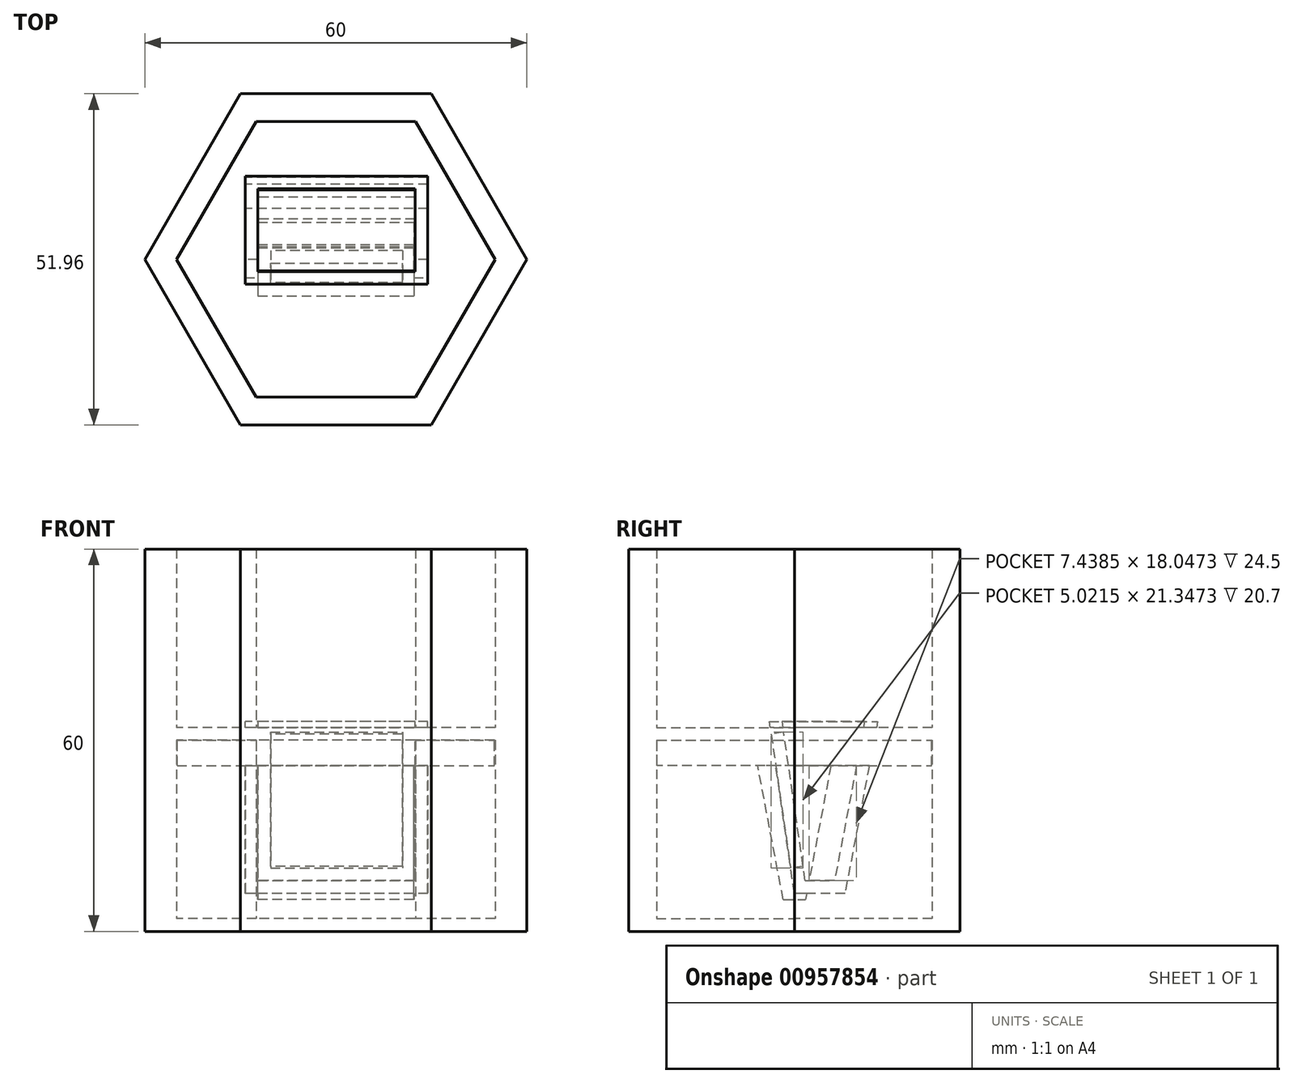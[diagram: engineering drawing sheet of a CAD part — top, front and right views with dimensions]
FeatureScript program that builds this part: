
annotation { "Feature Type Name" : "Feature", "Feature Type Description" : "" }
export const myFeature = defineFeature(function(context is Context, id is Id, definition is map)
    precondition{}
    {
        {
            var Q0;
            Q0=qCreatedBy(makeId("Top.planeOp"),FACE);
            var sketch = newSketch(context, id + "F0", { "sketchPlane" : qUnion([Q0])});
            skCircle(sketch, "E0.cCircle", {"center": v(0, 0) * mm, "radius": 30 * mm, "construction": true});
            skLineSegment(sketch, "E0.0", {"start": v(30, 0) * mm, "end": v(15, -25.98) * mm});
            skLineSegment(sketch, "E0.1", {"start": v(15, -25.98) * mm, "end": v(-15, -25.98) * mm});
            skLineSegment(sketch, "E0.2", {"start": v(-15, -25.98) * mm, "end": v(-30, 0) * mm});
            skLineSegment(sketch, "E0.3", {"start": v(-30, 0) * mm, "end": v(-15, 25.98) * mm});
            skLineSegment(sketch, "E0.4", {"start": v(-15, 25.98) * mm, "end": v(15, 25.98) * mm});
            skLineSegment(sketch, "E0.5", {"start": v(15, 25.98) * mm, "end": v(30, 0) * mm});
            skCircle(sketch, "E1.cCircle", {"center": v(0, 0) * mm, "radius": 25 * mm, "construction": true});
            skLineSegment(sketch, "E1.0", {"start": v(-25, 0) * mm, "end": v(-12.5, 21.65) * mm});
            skLineSegment(sketch, "E1.1", {"start": v(-12.5, 21.65) * mm, "end": v(12.5, 21.65) * mm});
            skLineSegment(sketch, "E1.2", {"start": v(12.5, 21.65) * mm, "end": v(25, 0) * mm});
            skLineSegment(sketch, "E1.3", {"start": v(25, 0) * mm, "end": v(12.5, -21.65) * mm});
            skLineSegment(sketch, "E1.4", {"start": v(12.5, -21.65) * mm, "end": v(-12.5, -21.65) * mm});
            skLineSegment(sketch, "E1.5", {"start": v(-12.5, -21.65) * mm, "end": v(-25, 0) * mm});
            skSolve(sketch);
        }
        {
            var Q0;
            Q0=makeQuery(id+"F0.imprint","IMPRINT",FACE,{"disambiguationData":[TD([[makeQuery(id+"F0.imprint","IMPRINT",EDGE,{"derivedFrom":sQuery(id+"F0.wireOp",EDGE,"E0.0")}),-1.0]])]});
            extrude(context, id + "F1", {"entities" : qUnion([Q0]), "endBound" : BoundingType.SYMMETRIC, "depth" : 60 * mm, "offsetDistance" : 25 * mm});
        }
        {
            var Q0;
            Q0=makeQuery(id+"F1.opExtrude","CAP_VERTEX",VERTEX,{"disambiguationData":[OSD([sQuery(id+"F0.wireOp",EDGE,"E0.4"),sQuery(id+"F0.wireOp",EDGE,"E0.5")])],"isStart":true});
            var Q1;
            Q1=makeQuery(id+"F1.opExtrude","CAP_VERTEX",VERTEX,{"disambiguationData":[OSD([sQuery(id+"F0.wireOp",EDGE,"E0.2"),sQuery(id+"F0.wireOp",EDGE,"E0.3")])],"isStart":true});
            var Q2;
            Q2=makeQuery(id+"F1.opExtrude","CAP_VERTEX",VERTEX,{"disambiguationData":[OSD([sQuery(id+"F0.wireOp",EDGE,"E0.0"),sQuery(id+"F0.wireOp",EDGE,"E0.1")])],"isStart":true});
            cPlane(context, id + "F2", {"entities" : qUnion([Q0, Q1, Q2]), "cplaneType" : CPlaneType.THREE_POINT, "offset" : 25 * mm, "width" : 150 * mm, "height" : 150 * mm});
        }
        {
            var Q0;
            Q0=qCreatedBy(id+"F2.planeOp",FACE);
            var sketch = newSketch(context, id + "F3", { "sketchPlane" : qUnion([Q0])});
            skLineSegment(sketch, "E2.0", {"start": v(-12.5, -21.65) * mm, "end": v(12.5, -21.65) * mm});
            skLineSegment(sketch, "E3.0", {"start": v(12.5, -21.65) * mm, "end": v(25, 0) * mm});
            skLineSegment(sketch, "E4.0", {"start": v(25, 0) * mm, "end": v(12.5, 21.65) * mm});
            skPoint(sketch, "E5.0", {"position": v(0, 21.65) * mm});
            skLineSegment(sketch, "E6.0", {"start": v(-12.5, 21.65) * mm, "end": v(-25, 0) * mm});
            skLineSegment(sketch, "E7.0", {"start": v(-25, 0) * mm, "end": v(-12.5, -21.65) * mm});
            skLineSegment(sketch, "E8.0", {"start": v(12.5, 21.65) * mm, "end": v(-12.5, 21.65) * mm});
            skSolve(sketch);
        }
        {
            var Q0;
            Q0=makeQuery(id+"F3.imprint","IMPRINT",FACE,{"disambiguationData":[TD([[makeQuery(id+"F3.imprint","IMPRINT",EDGE,{"derivedFrom":sQuery(id+"F3.wireOp",EDGE,"E2.0")}),1.0]])]});
            extrude(context, id + "F4", {"entities" : qUnion([Q0]), "operationType" : NewBodyOperationType.ADD, "oppositeDirection" : true, "depth" : 2 * mm, "offsetDistance" : 25 * mm});
        }
        {
            var Q0;
            Q0=qCreatedBy(makeId("Top.planeOp"),FACE);
            var sketch = newSketch(context, id + "F5", { "sketchPlane" : qUnion([Q0])});
            skLineSegment(sketch, "E9.0.0", {"start": v(30, 0) * mm, "end": v(15, 25.98) * mm});
            skLineSegment(sketch, "E9.0.1", {"start": v(15, 25.98) * mm, "end": v(-15, 25.98) * mm});
            skLineSegment(sketch, "E9.0.2", {"start": v(-15, 25.98) * mm, "end": v(-30, 0) * mm});
            skLineSegment(sketch, "E9.0.3", {"start": v(-30, 0) * mm, "end": v(-15, -25.98) * mm});
            skLineSegment(sketch, "E9.0.4", {"start": v(-15, -25.98) * mm, "end": v(15, -25.98) * mm});
            skLineSegment(sketch, "E9.0.5", {"start": v(15, -25.98) * mm, "end": v(30, 0) * mm});
            skCircle(sketch, "E10.cCircle", {"center": v(0, 0) * mm, "radius": 24.9 * mm, "construction": true});
            skLineSegment(sketch, "E10.0", {"start": v(-24.9, 0) * mm, "end": v(-12.45, 21.56) * mm});
            skLineSegment(sketch, "E10.1", {"start": v(-12.45, 21.56) * mm, "end": v(12.45, 21.56) * mm});
            skLineSegment(sketch, "E10.2", {"start": v(12.45, 21.56) * mm, "end": v(24.9, 0) * mm});
            skLineSegment(sketch, "E10.3", {"start": v(24.9, 0) * mm, "end": v(12.45, -21.56) * mm});
            skLineSegment(sketch, "E10.4", {"start": v(12.45, -21.56) * mm, "end": v(-12.45, -21.56) * mm});
            skLineSegment(sketch, "E10.5", {"start": v(-12.45, -21.56) * mm, "end": v(-24.9, 0) * mm});
            skSolve(sketch);
        }
        {
            var Q0;
            Q0=makeQuery(id+"F5.imprint","IMPRINT",FACE,{"disambiguationData":[TD([[makeQuery(id+"F5.imprint","IMPRINT",EDGE,{"derivedFrom":sQuery(id+"F5.wireOp",EDGE,"E10.0")}),-1.0]])]});
            extrude(context, id + "F6", {"entities" : qUnion([Q0]), "oppositeDirection" : true, "depth" : 4 * mm, "offsetDistance" : 25 * mm});
        }
        {
            var Q0;
            Q0=makeQuery(id+"F5.imprint","IMPRINT",FACE,{"disambiguationData":[TD([[makeQuery(id+"F5.imprint","IMPRINT",EDGE,{"derivedFrom":sQuery(id+"F5.wireOp",EDGE,"E9.0.0")}),1.0]])]});
            var Q1;
            Q1=makeQuery(id+"F5.imprint","IMPRINT",FACE,{"disambiguationData":[TD([[makeQuery(id+"F5.imprint","IMPRINT",EDGE,{"derivedFrom":sQuery(id+"F5.wireOp",EDGE,"E10.0")}),-1.0]])]});
            extrude(context, id + "F7", {"entities" : qUnion([Q0, Q1]), "operationType" : NewBodyOperationType.ADD, "depth" : 2 * mm, "offsetDistance" : 25 * mm});
        }
        {
            var Q0;
            Q0=qCreatedBy(makeId("Top.planeOp"),FACE);
            var sketch = newSketch(context, id + "F8", { "sketchPlane" : qUnion([Q0])});
            skLineSegment(sketch, "E11.bottom", {"start": v(12.25, 6.5) * mm, "end": v(-12.25, 6.5) * mm});
            skLineSegment(sketch, "E11.top", {"start": v(12.25, -6.5) * mm, "end": v(-12.25, -6.5) * mm});
            skLineSegment(sketch, "E11.left", {"start": v(12.25, 6.5) * mm, "end": v(12.25, -6.5) * mm});
            skLineSegment(sketch, "E11.right", {"start": v(-12.25, 6.5) * mm, "end": v(-12.25, -6.5) * mm});
            skPoint(sketch, "E11.middle", {"position": v(0, 0) * mm});
            skSolve(sketch);
        }
        {
            var Q0;
            Q0=qCreatedBy(makeId("Top.planeOp"),FACE);
            cPlane(context, id + "F9", {"entities" : qUnion([Q0]), "cplaneType" : CPlaneType.OFFSET, "offset" : 25 * mm, "oppositeDirection" : true, "width" : 150 * mm, "height" : 150 * mm});
        }
        {
            var Q0;
            Q0=qCreatedBy(id+"F9.planeOp",FACE);
            var sketch = newSketch(context, id + "F10", { "sketchPlane" : qUnion([Q0])});
            skLineSegment(sketch, "E12.bottom", {"start": v(12.25, -1.75) * mm, "end": v(-12.25, -1.75) * mm});
            skLineSegment(sketch, "E12.top", {"start": v(12.25, 1.75) * mm, "end": v(-12.25, 1.75) * mm});
            skLineSegment(sketch, "E12.left", {"start": v(12.25, -1.75) * mm, "end": v(12.25, 1.75) * mm});
            skLineSegment(sketch, "E12.right", {"start": v(-12.25, -1.75) * mm, "end": v(-12.25, 1.75) * mm});
            skPoint(sketch, "E12.middle", {"position": v(0, 0) * mm});
            skSolve(sketch);
        }
        {
            var Q0;
            Q0=sQuery(id+"F8.wireOp",VERTEX,"E11.bottom.end");
            var Q1;
            Q1=sQuery(id+"F8.wireOp",VERTEX,"E11.top.end");
            var Q2;
            Q2=sQuery(id+"F10.wireOp",VERTEX,"E12.bottom.end");
            cPlane(context, id + "F11", {"entities" : qUnion([Q0, Q1, Q2]), "cplaneType" : CPlaneType.THREE_POINT, "offset" : 25 * mm, "width" : 150 * mm, "height" : 150 * mm});
        }
        {
            var Q0;
            Q0=qCreatedBy(id+"F11.planeOp",FACE);
            var sketch = newSketch(context, id + "F12", { "sketchPlane" : qUnion([Q0])});
            skLineSegment(sketch, "E13.0", {"start": v(-6.5, 0) * mm, "end": v(6.5, 0) * mm});
            skLineSegment(sketch, "E14.0", {"start": v(1.75, -25) * mm, "end": v(-1.75, -25) * mm});
            skLineSegment(sketch, "E15", {"start": v(-6.5, 0) * mm, "end": v(-1.75, -25) * mm});
            skLineSegment(sketch, "E16", {"start": v(1.75, -25) * mm, "end": v(6.5, 0) * mm});
            skSolve(sketch);
        }
        {
            var Q0;
            Q0=makeQuery(id+"F12.imprint","IMPRINT",FACE,{"disambiguationData":[TD([[makeQuery(id+"F12.imprint","IMPRINT",EDGE,{"derivedFrom":sQuery(id+"F12.wireOp",EDGE,"E13.0")}),-1.0]])]});
            extrude(context, id + "F13", {"entities" : qUnion([Q0]), "oppositeDirection" : true, "depth" : 24.5 * mm, "offsetDistance" : 25 * mm});
        }
        {
            var Q0;
            Q0=qCreatedBy(id+"F11.planeOp",FACE);
            var sketch = newSketch(context, id + "F14", { "sketchPlane" : qUnion([Q0])});
            skLineSegment(sketch, "E17.0", {"start": v(-11.07, 2.96) * mm, "end": v(1.93, 2.96) * mm});
            skLineSegment(sketch, "E18.0", {"start": v(-1.7, -22.04) * mm, "end": v(-6.32, -22.05) * mm});
            skLineSegment(sketch, "E19", {"start": v(-11.07, 2.96) * mm, "end": v(-6.32, -22.05) * mm});
            skLineSegment(sketch, "E20", {"start": v(-1.7, -22.04) * mm, "end": v(1.93, 2.96) * mm});
            skLineSegment(sketch, "E21", {"start": v(-11.07, 2.96) * mm, "end": v(-13.07, 2.96) * mm});
            skLineSegment(sketch, "E22", {"start": v(-13.07, 2.96) * mm, "end": v(-7.94, -24.05) * mm});
            skLineSegment(sketch, "E23", {"start": v(-7.94, -24.05) * mm, "end": v(0, -24.04) * mm});
            skLineSegment(sketch, "E24", {"start": v(0, -24.04) * mm, "end": v(3.93, 2.96) * mm});
            skLineSegment(sketch, "E25", {"start": v(3.93, 2.96) * mm, "end": v(1.93, 2.96) * mm});
            skSolve(sketch);
        }
        {
            var Q0;
            Q0=makeQuery(id+"F14.imprint","IMPRINT",FACE,{"disambiguationData":[TD([[makeQuery(id+"F14.imprint","IMPRINT",EDGE,{"derivedFrom":sQuery(id+"F14.wireOp",EDGE,"E18.0")}),1.0]])]});
            extrude(context, id + "F15", {"entities" : qUnion([Q0]), "oppositeDirection" : true, "depth" : 24.7 * mm, "offsetDistance" : 25 * mm});
        }
        {
            var Q0;
            Q0=makeQuery(id+"F15.opExtrude","CAP_FACE",FACE,{"disambiguationData":[OSD([sQuery(id+"F14.wireOp",EDGE,"E18.0"),sQuery(id+"F14.wireOp",EDGE,"E19"),sQuery(id+"F14.wireOp",EDGE,"E20"),sQuery(id+"F14.wireOp",EDGE,"E21"),sQuery(id+"F14.wireOp",EDGE,"E22"),sQuery(id+"F14.wireOp",EDGE,"E23"),sQuery(id+"F14.wireOp",EDGE,"E24"),sQuery(id+"F14.wireOp",EDGE,"E25")])],"isStart":true});
            extrude(context, id + "F16", {"entities" : qUnion([Q0]), "operationType" : NewBodyOperationType.ADD, "depth" : 2 * mm, "offsetDistance" : 25 * mm});
        }
        {
            var Q0;
            Q0 = qSketchRegion(id + "F14", true);
            extrude(context, id + "F17", {"entities" : qUnion([Q0]), "operationType" : NewBodyOperationType.ADD, "depth" : 2 * mm, "offsetDistance" : 25 * mm});
        }
        {
            var Q0;
            Q0=makeQuery(id+"F15.opExtrude","CAP_VERTEX",VERTEX,{"disambiguationData":[OSD([sQuery(id+"F14.wireOp",EDGE,"E22"),sQuery(id+"F14.wireOp",EDGE,"E23")])],"isStart":false});
            var Q1;
            Q1=makeQuery(id+"F15.opExtrude","CAP_VERTEX",VERTEX,{"disambiguationData":[OSD([sQuery(id+"F14.wireOp",EDGE,"E21"),sQuery(id+"F14.wireOp",EDGE,"E22")])],"isStart":false});
            var Q2;
            Q2=makeQuery(id+"F15.opExtrude","CAP_VERTEX",VERTEX,{"disambiguationData":[OSD([sQuery(id+"F14.wireOp",EDGE,"E24"),sQuery(id+"F14.wireOp",EDGE,"E25")])],"isStart":false});
            cPlane(context, id + "F18", {"entities" : qUnion([Q0, Q1, Q2]), "cplaneType" : CPlaneType.THREE_POINT, "offset" : 25 * mm, "width" : 150 * mm, "height" : 150 * mm});
        }
        {
            var Q0;
            Q0=qCreatedBy(id+"F18.planeOp",FACE);
            var sketch = newSketch(context, id + "F19", { "sketchPlane" : qUnion([Q0])});
            skLineSegment(sketch, "E26.0", {"start": v(-13.07, 2.96) * mm, "end": v(-7.94, -24.05) * mm});
            skLineSegment(sketch, "E27.0", {"start": v(0, -24.04) * mm, "end": v(3.93, 2.96) * mm});
            skLineSegment(sketch, "E28.0", {"start": v(-7.94, -24.05) * mm, "end": v(0, -24.04) * mm});
            skLineSegment(sketch, "E29", {"start": v(-13.07, 2.96) * mm, "end": v(3.93, 2.96) * mm});
            skSolve(sketch);
        }
        {
            var Q0;
            Q0=makeQuery(id+"F19.imprint","IMPRINT",FACE,{"disambiguationData":[TD([[makeQuery(id+"F19.imprint","IMPRINT",EDGE,{"derivedFrom":sQuery(id+"F19.wireOp",EDGE,"E26.0")}),1.0]])]});
            extrude(context, id + "F20", {"entities" : qUnion([Q0]), "operationType" : NewBodyOperationType.ADD, "oppositeDirection" : true, "depth" : 2 * mm, "offsetDistance" : 25 * mm});
        }
        {
            var Q0;
            Q0=makeQuery(id+"F16.opExtrude","CAP_VERTEX",VERTEX,{"disambiguationData":[OSD([sQuery(id+"F14.wireOp",EDGE,"E24"),sQuery(id+"F14.wireOp",EDGE,"E25")])],"isStart":false});
            var Q1;
            Q1=makeQuery(id+"F20.opExtrude","CAP_VERTEX",VERTEX,{"disambiguationData":[OSD([sQuery(id+"F19.wireOp",EDGE,"E27.0"),sQuery(id+"F19.wireOp",EDGE,"E29")])],"isStart":false});
            var Q2;
            Q2=makeQuery(id+"F20.opExtrude","CAP_VERTEX",VERTEX,{"disambiguationData":[OSD([sQuery(id+"F19.wireOp",EDGE,"E27.0"),sQuery(id+"F19.wireOp",EDGE,"E28.0")])],"isStart":false});
            cPlane(context, id + "F21", {"entities" : qUnion([Q0, Q1, Q2]), "cplaneType" : CPlaneType.THREE_POINT, "offset" : 25 * mm, "width" : 150 * mm, "height" : 150 * mm});
        }
        {
            var Q0;
            Q0=qCreatedBy(id+"F21.planeOp",FACE);
            var sketch = newSketch(context, id + "F22", { "sketchPlane" : qUnion([Q0])});
            skLineSegment(sketch, "E30.0", {"start": v(-14.25, -23.79) * mm, "end": v(-14.25, 3.5) * mm});
            skLineSegment(sketch, "E31.0", {"start": v(14.45, -23.79) * mm, "end": v(14.45, 3.5) * mm});
            skLineSegment(sketch, "E32", {"start": v(-14.25, -23.79) * mm, "end": v(14.45, -23.79) * mm});
            skLineSegment(sketch, "E33", {"start": v(-14.25, 3.5) * mm, "end": v(-10.25, 3.5) * mm});
            skLineSegment(sketch, "E34", {"start": v(-10.25, -19.79) * mm, "end": v(10.45, -19.79) * mm});
            skLineSegment(sketch, "E35", {"start": v(10.45, 3.5) * mm, "end": v(14.45, 3.5) * mm});
            skLineSegment(sketch, "E36", {"start": v(-10.25, 3.5) * mm, "end": v(10.45, 3.5) * mm});
            skLineSegment(sketch, "E37", {"start": v(10.45, 1.5) * mm, "end": v(-10.25, 1.5) * mm});
            skLineSegment(sketch, "E38", {"start": v(-10.25, 1.5) * mm, "end": v(-10.25, -19.79) * mm});
            skLineSegment(sketch, "E39", {"start": v(10.45, 1.5) * mm, "end": v(10.45, -19.79) * mm});
            skSolve(sketch);
        }
        {
            var Q0;
            Q0=makeQuery(id+"F22.imprint","IMPRINT",FACE,{"disambiguationData":[TD([[makeQuery(id+"F22.imprint","IMPRINT",EDGE,{"derivedFrom":sQuery(id+"F22.wireOp",EDGE,"E34")}),1.0]])]});
            var Q1;
            {var subQ0=sQuery(id+"F14.wireOp",EDGE,"E20");Q1=makeQuery(id+"F16.boolean.opBoolean","MERGE",FACE,{"derivedFrom":[makeQuery(id+"F15.opExtrude","SWEPT_FACE",FACE,{"disambiguationData":[OSD([subQ0])]}),makeQuery(id+"F16.opExtrude","SWEPT_FACE",FACE,{"disambiguationData":[OSD([subQ0])]})]});}
            extrude(context, id + "F23", {"entities" : qUnion([Q0]), "operationType" : NewBodyOperationType.REMOVE, "endBound" : BoundingType.UP_TO_SURFACE, "oppositeDirection" : true, "depth" : 25 * mm, "endBoundEntityFace" : qUnion([Q1]), "offsetDistance" : 25 * mm, "offsetOppositeDirection" : true});
        }
    });
